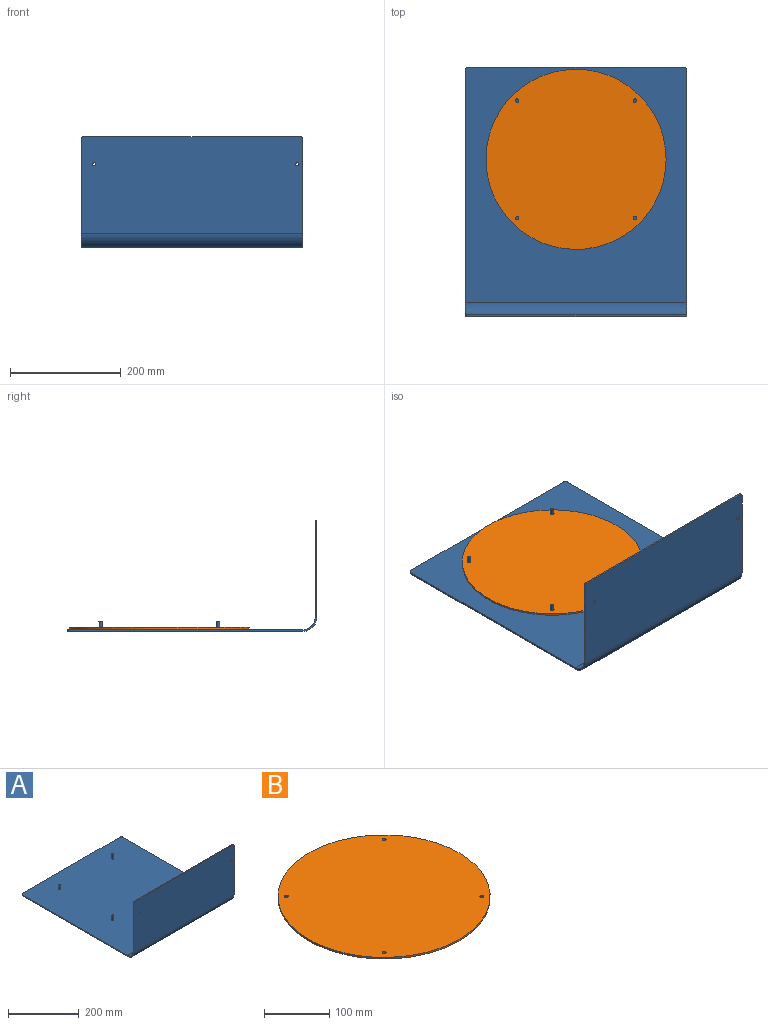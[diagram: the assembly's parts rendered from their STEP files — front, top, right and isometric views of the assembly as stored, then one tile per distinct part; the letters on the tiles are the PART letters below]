
ASSEMBLY  parts=2 mates=1
PART A: 24 faces, bbox 400x450x200 mm
  f0: plane 400x175mm, normal (0,1,0), area 69930.8mm2, adj f1,f7,f8,f9,f19,f21,f22,f23
  f1: plane 390x3mm, normal (0,0,1), area 1170mm2, adj f0,f2,f19,f21
  f2: plane 400x175mm, normal (0,-1,0), area 69930.8mm2, adj f1,f3,f8,f9,f19,f21,f22,f23
  f3: cylinder r=25mm len=400mm, axis (-1,0,0), area 15708mm2, adj f2,f4,f8,f9
  f4: plane 425x400mm, normal (0,0,-1), area 169989.3mm2, adj f3,f5,f8,f9,f18,f20
  f5: plane 390x3mm, normal (0,1,0), area 1170mm2, adj f4,f6,f18,f20
  f6: plane 425x400mm, normal (0,0,1), area 169876.2mm2, adj f5,f7,f8,f9,f10,f12,f14,f16
  f7: cylinder r=22mm len=400mm, axis (-1,0,0), area 13823mm2, adj f0,f6,f8,f9
  f8: plane 445x195mm, normal (1,0,0), area 1880.7mm2, adj f0,f2,f3,f4,f6,f7,f20,f21
  f9: plane 445x195mm, normal (-1,0,0), area 1880.7mm2, adj f0,f2,f3,f4,f6,f7,f18,f19
  f10: cylinder r=3mm len=15mm, axis (0,0,-1), area 282.7mm2, adj f6,f11
  f11: plane 6x6mm, normal (0,0,1), area 28.3mm2, adj f10
  f12: cylinder r=3mm len=15mm, axis (0,0,-1), area 282.7mm2, adj f6,f13
  f13: plane 6x6mm, normal (0,0,1), area 28.3mm2, adj f12
  f14: cylinder r=3mm len=15mm, axis (0,0,-1), area 282.7mm2, adj f6,f15
  f15: plane 6x6mm, normal (0,0,1), area 28.3mm2, adj f14
  f16: cylinder r=3mm len=15mm, axis (0,0,-1), area 282.7mm2, adj f6,f17
  f17: plane 6x6mm, normal (0,0,1), area 28.3mm2, adj f16
  f18: cylinder r=5mm len=5mm, axis (0,0,1), area 23.6mm2, adj f4,f5,f6,f9
  f19: cylinder r=5mm len=5mm, axis (0,-1,0), area 23.6mm2, adj f0,f1,f2,f9
  f20: cylinder r=5mm len=5mm, axis (0,0,-1), area 23.6mm2, adj f4,f5,f6,f8
  f21: cylinder r=5mm len=5mm, axis (0,1,0), area 23.6mm2, adj f0,f1,f2,f8
  f22: cylinder r=3.05mm len=6.1mm, axis (0,1,0), area 57.5mm2, adj f0,f2
  f23: cylinder r=3.05mm len=6.1mm, axis (0,1,0), area 57.5mm2, adj f0,f2
PART B: 7 faces, bbox 325x325x3 mm
  f0: cylinder r=3.05mm len=6.1mm, axis (0,0,1), area 57.5mm2, adj f5,f6
  f1: cylinder r=3.05mm len=6.1mm, axis (0,0,1), area 57.5mm2, adj f5,f6
  f2: cylinder r=3.05mm len=6.1mm, axis (0,0,1), area 57.5mm2, adj f5,f6
  f3: cylinder r=3.05mm len=6.1mm, axis (0,0,1), area 57.5mm2, adj f5,f6
  f4: cylinder r=162.5mm len=325mm, axis (0,0,1), area 3063.1mm2, adj f5,f6
  f5: plane 325x325mm, normal (0,0,-1), area 82840.8mm2, adj f0,f1,f2,f3,f4
  f6: plane 325x325mm, normal (0,0,1), area 82840.8mm2, adj f0,f1,f2,f3,f4
PLACE A t=(236.28,243.11,94.19)mm
PLACE B t=(436.3,527.06,101.46)mm
MATE slider B.f2 <-> A.f14  axis (0,0,1) through (542.38,421.01,101.46)mm
